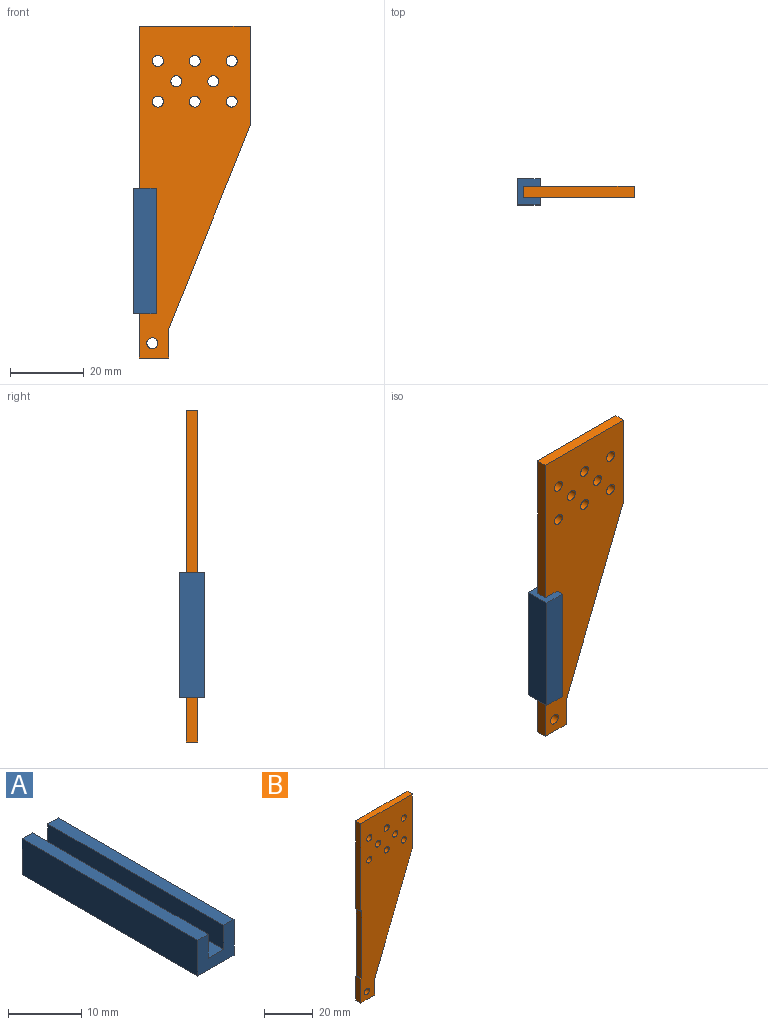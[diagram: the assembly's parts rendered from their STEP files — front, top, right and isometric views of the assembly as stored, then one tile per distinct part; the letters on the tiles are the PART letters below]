
ASSEMBLY  parts=2 mates=1
PART A: 10 faces, bbox 7x34x6 mm
  f0: plane 34x6mm, normal (-1,0,0), area 204mm2, adj f1,f7,f8,f9
  f1: plane 34x7mm, normal (0,0,-1), area 238mm2, adj f0,f2,f8,f9
  f2: plane 34x6mm, normal (1,0,0), area 204mm2, adj f1,f3,f8,f9
  f3: plane 34x2mm, normal (0,0,1), area 68mm2, adj f2,f4,f8,f9
  f4: plane 34x4mm, normal (-1,0,0), area 136mm2, adj f3,f5,f8,f9
  f5: plane 34x3mm, normal (0,0,1), area 102mm2, adj f4,f6,f8,f9
  f6: plane 34x4mm, normal (1,0,0), area 136mm2, adj f5,f7,f8,f9
  f7: plane 34x2mm, normal (0,0,1), area 68mm2, adj f0,f6,f8,f9
  f8: plane 7x6mm, normal (0,-1,0), area 30mm2, adj f0,f1,f2,f3,f4,f5,f6,f7
  f9: plane 7x6mm, normal (0,1,0), area 30mm2, adj f0,f1,f2,f3,f4,f5,f6,f7
PART B: 21 faces, bbox 30x3x90 mm
  f0: plane 12x3mm, normal (-1,0,0), area 36mm2, adj f1,f9,f10,f11
  f1: plane 8x3mm, normal (0,0,-1), area 24mm2, adj f0,f2,f10,f11
  f2: plane 8x3mm, normal (1,0,0), area 24mm2, adj f1,f3,f10,f11
  f3: plane 55x22mm, normal (0.93,0,-0.37), area 177.7mm2, adj f2,f4,f10,f11
  f4: plane 27x3mm, normal (1,0,0), area 81mm2, adj f3,f5,f10,f11
  f5: plane 30x3mm, normal (0,0,1), area 90mm2, adj f4,f6,f10,f11
  f6: plane 44x3mm, normal (-1,0,0), area 132mm2, adj f5,f7,f10,f11
  f7: plane 3x0.5mm, normal (0,0,-1), area 1.5mm2, adj f6,f8,f10,f11
  f8: plane 34x3mm, normal (-1,0,0), area 102mm2, adj f7,f9,f10,f11
  f9: plane 3x0.5mm, normal (0,0,1), area 1.5mm2, adj f0,f8,f10,f11
  f10: plane 90x30mm, normal (0,-1,0), area 1838.4mm2, adj f0,f1,f2,f3,f4,f5,f6,f7
  f11: plane 90x30mm, normal (0,1,0), area 1838.4mm2, adj f0,f1,f2,f3,f4,f5,f6,f7
  f12: cylinder r=1.5mm len=3mm, axis (0,1,0), area 28.3mm2, adj f10,f11
  f13: cylinder r=1.5mm len=3mm, axis (0,1,0), area 28.3mm2, adj f10,f11
  f14: cylinder r=1.5mm len=3mm, axis (0,1,0), area 28.3mm2, adj f10,f11
  f15: cylinder r=1.5mm len=3mm, axis (0,1,0), area 28.3mm2, adj f10,f11
  f16: cylinder r=1.5mm len=3mm, axis (0,1,0), area 28.3mm2, adj f10,f11
  f17: cylinder r=1.5mm len=3mm, axis (0,1,0), area 28.3mm2, adj f10,f11
  f18: cylinder r=1.5mm len=3mm, axis (0,1,0), area 28.3mm2, adj f10,f11
  f19: cylinder r=1.5mm len=3mm, axis (0,1,0), area 28.3mm2, adj f10,f11
  f20: cylinder r=1.5mm len=3mm, axis (0,1,0), area 28.3mm2, adj f10,f11
PLACE A rot(axis=(-0.58,0.58,-0.58),120deg) t=(-198.28,56.37,-96.58)mm
PLACE B t=(-196.78,54.37,-108.58)mm fixed
MATE fastened A.f9 <-> B.f9  axis (0,0,-1) through (-196.28,54.37,-96.58)mm
